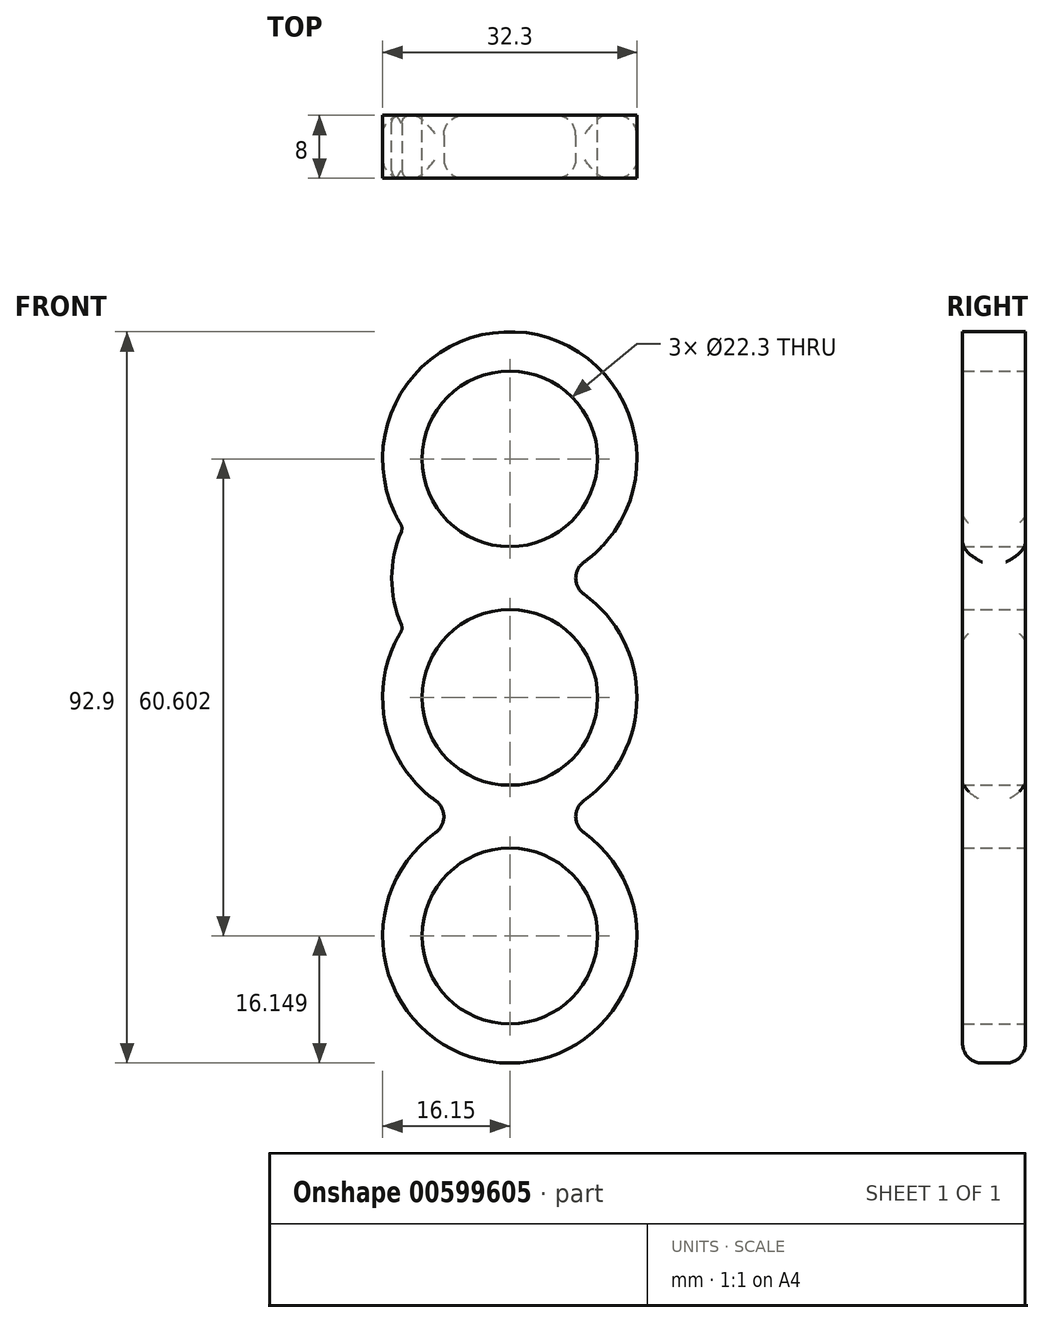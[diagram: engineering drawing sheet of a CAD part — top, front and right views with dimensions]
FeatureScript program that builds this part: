
annotation { "Feature Type Name" : "Feature", "Feature Type Description" : "" }
export const myFeature = defineFeature(function(context is Context, id is Id, definition is map)
    precondition{}
    {
        {
            var Q0;
            Q0=qCreatedBy(makeId("Front.planeOp"),FACE);
            var sketch = newSketch(context, id + "F0", { "sketchPlane" : qUnion([Q0])});
            skCircle(sketch, "E0", {"center": v(0, 0) * mm, "radius": 11.15 * mm});
            skCircle(sketch, "E1", {"center": v(0, 30.3) * mm, "radius": 11.15 * mm});
            skArc(sketch, "E2", {"start": v(-13.57, 8.76) * mm, "mid": v(-15, 15.15) * mm, "end": v(-13.57, 21.54) * mm});
            skArc(sketch, "E3", {"start": v(-15.87, 3.02) * mm, "mid": v(-19.97, 15.15) * mm, "end": v(-15.87, 27.28) * mm});
            skArc(sketch, "E4.1.1", {"start": v(15.87, -3.02) * mm, "mid": v(19.97, -15.15) * mm, "end": v(15.87, -27.28) * mm});
            skCircle(sketch, "E4.1.2", {"center": v(0, -30.3) * mm, "radius": 11.15 * mm});
            skArc(sketch, "E4.1.3", {"start": v(13.57, -8.76) * mm, "mid": v(15, -15.15) * mm, "end": v(13.57, -21.54) * mm});
            skArc(sketch, "E5.0", {"start": v(5.6, 15.15) * mm, "mid": v(0, 46.45) * mm, "end": v(-5.6, 15.15) * mm});
            skArc(sketch, "E6.0", {"start": v(-5.6, 15.15) * mm, "mid": v(-16.15, 0) * mm, "end": v(-5.6, -15.15) * mm});
            skArc(sketch, "E7.0", {"start": v(-5.6, -15.15) * mm, "mid": v(0, -46.45) * mm, "end": v(5.6, -15.15) * mm});
            skPoint(sketch, "E8.orphan", {"position": v(-15.02, 28.31) * mm});
            skPoint(sketch, "E9.orphan", {"position": v(-12.86, 22.87) * mm});
            skPoint(sketch, "E10.orphan", {"position": v(-15.02, 1.99) * mm});
            skArc(sketch, "E11.trimOffspring", {"start": v(5.6, -15.15) * mm, "mid": v(16.15, 0) * mm, "end": v(5.6, 15.15) * mm});
            skPoint(sketch, "E12.orphan", {"position": v(-13.03, 7.72) * mm});
            skPoint(sketch, "E13.orphan", {"position": v(13.03, -7.72) * mm});
            skPoint(sketch, "E14.orphan", {"position": v(12.86, -22.87) * mm});
            skSolve(sketch);
        }
        {
            var Q0;
            {var subQ0=sQuery(id+"F0.wireOp",EDGE,"E4.1.1");Q0=makeQuery(id+"F0.imprint","IMPRINT",FACE,{"disambiguationData":[TD([[makeQuery(id+"F0.imprint","IMPRINT",EDGE,{"derivedFrom":subQ0}),-1.0]])]});}
            var Q1;
            {var subQ0=sQuery(id+"F0.wireOp",EDGE,"E2");Q1=makeQuery(id+"F0.imprint","IMPRINT",FACE,{"disambiguationData":[TD([[makeQuery(id+"F0.imprint","IMPRINT",EDGE,{"derivedFrom":subQ0}),1.0]])]});}
            var Q2;
            Q2=makeQuery(id+"F0.imprint","IMPRINT",FACE,{"disambiguationData":[TD([[makeQuery(id+"F0.imprint","IMPRINT",EDGE,{"derivedFrom":sQuery(id+"F0.wireOp",EDGE,"E0")}),-1.0]])]});
            extrude(context, id + "F1", {"entities" : qUnion([Q0, Q1, Q2]), "depth" : 8 * mm, "offsetDistance" : 25.4 * mm});
        }
        {
            var Q0;
            {var subQ0=sQuery(id+"F0.wireOp",EDGE,"E7.0");Q0=makeQuery(id+"F1.opExtrude","SWEPT_FACE",FACE,{"disambiguationData":[OSD([subQ0]),TDD([makeQuery(id+"F0.imprint","IMPRINT",EDGE,{"disambiguationData":[TD([[makeQuery(id+"F0.imprint","INTERSECT",VERTEX,{"derivedFrom":[sQuery(id+"F0.wireOp",EDGE,"E4.1.1"),subQ0]}),1.0]])],"derivedFrom":subQ0})])]});}
            var Q1;
            {var subQ0=sQuery(id+"F0.wireOp",EDGE,"E11.trimOffspring");Q1=makeQuery(id+"F1.opExtrude","SWEPT_FACE",FACE,{"disambiguationData":[OSD([subQ0]),TDD([makeQuery(id+"F0.imprint","IMPRINT",EDGE,{"disambiguationData":[TD([[makeQuery(id+"F0.imprint","INTERSECT",VERTEX,{"derivedFrom":[sQuery(id+"F0.wireOp",EDGE,"E4.1.1"),subQ0]}),-1.0]])],"derivedFrom":subQ0})])]});}
            var Q2;
            Q2=makeQuery(id+"F1.opExtrude","SWEPT_FACE",FACE,{"disambiguationData":[OSD([sQuery(id+"F0.wireOp",EDGE,"E3")])]});
            fillet(context, id + "F2", {"entities" : qUnion([Q0, Q1, Q2]), "radius" : 2.5 * mm, "tangentPropagation" : true, "allowEdgeOverflow" : false});
        }
        {
            var Q0;
            Q0=makeQuery(id+"F1.opExtrude","SWEPT_FACE",FACE,{"disambiguationData":[OSD([sQuery(id+"F0.wireOp",EDGE,"E2")])]});
            var Q1;
            Q1=makeQuery(id+"F1.opExtrude","SWEPT_FACE",FACE,{"disambiguationData":[OSD([sQuery(id+"F0.wireOp",EDGE,"E4.1.3")])]});
            fillet(context, id + "F3", {"entities" : qUnion([Q0, Q1]), "radius" : 1 * mm, "tangentPropagation" : true, "allowEdgeOverflow" : false});
        }
    });
